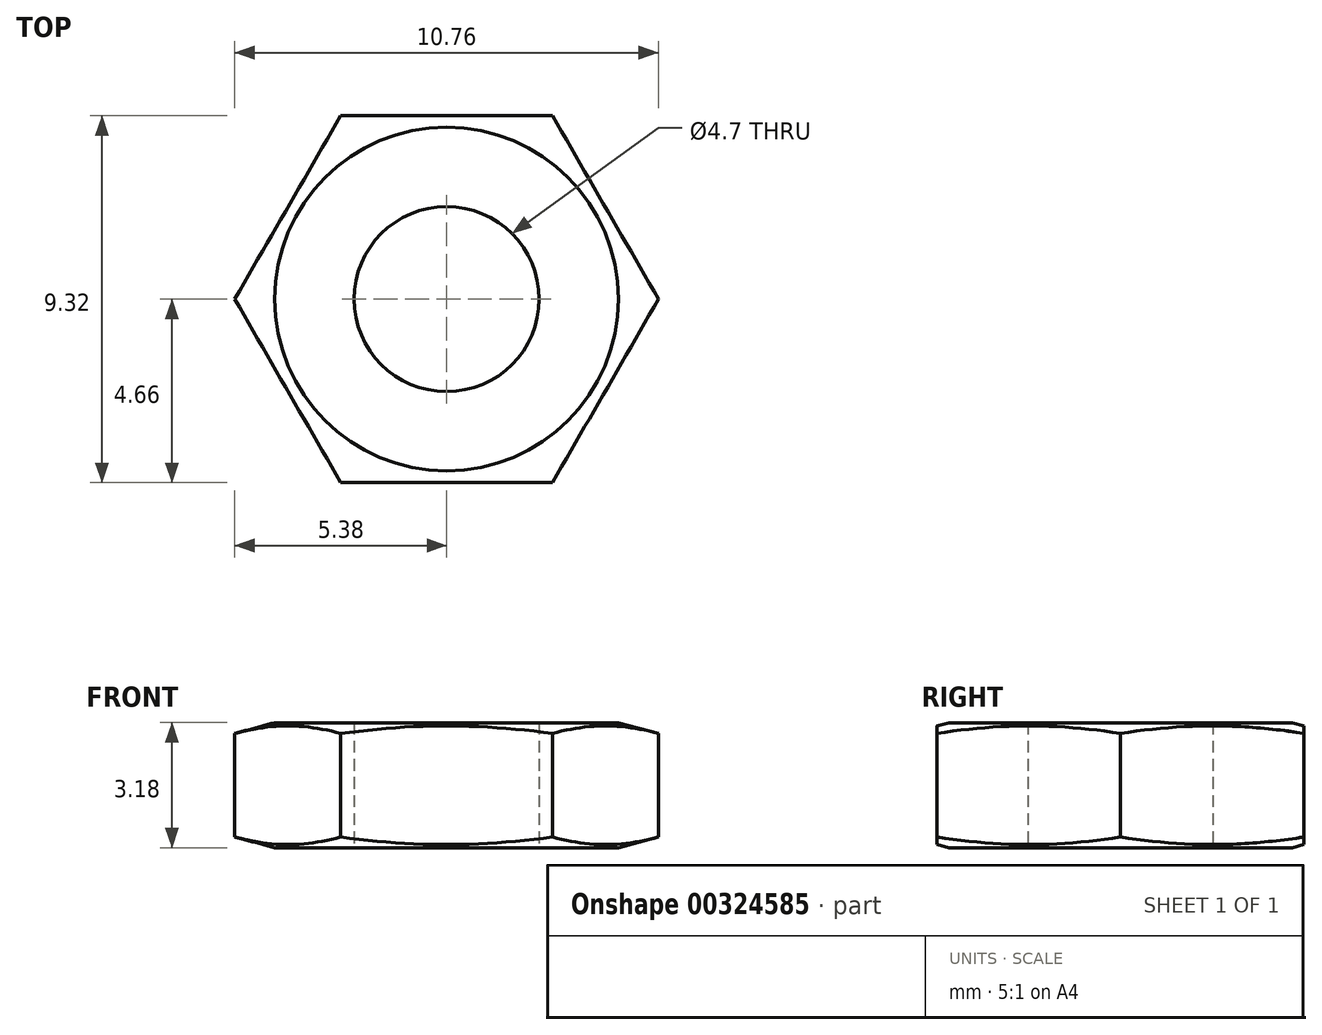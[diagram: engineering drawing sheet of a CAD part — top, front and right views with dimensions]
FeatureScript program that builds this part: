
annotation { "Feature Type Name" : "Feature", "Feature Type Description" : "" }
export const myFeature = defineFeature(function(context is Context, id is Id, definition is map)
    precondition{}
    {
        {
            var Q0;
            Q0=qCreatedBy(makeId("Top.planeOp"),FACE);
            var sketch = newSketch(context, id + "F0", { "sketchPlane" : qUnion([Q0])});
            skCircle(sketch, "E0.cCircle", {"center": v(0, 0) * mm, "radius": 4.66 * mm, "construction": true});
            skLineSegment(sketch, "E0.0", {"start": v(2.7, 4.66) * mm, "end": v(5.38, 0) * mm});
            skLineSegment(sketch, "E0.1", {"start": v(5.38, 0) * mm, "end": v(2.7, -4.66) * mm});
            skLineSegment(sketch, "E0.2", {"start": v(2.7, -4.66) * mm, "end": v(-2.7, -4.66) * mm});
            skLineSegment(sketch, "E0.3", {"start": v(-2.7, -4.66) * mm, "end": v(-5.38, 0) * mm});
            skLineSegment(sketch, "E0.4", {"start": v(-5.38, 0) * mm, "end": v(-2.7, 4.66) * mm});
            skLineSegment(sketch, "E0.5", {"start": v(-2.7, 4.66) * mm, "end": v(2.7, 4.66) * mm});
            skPoint(sketch, "E0.0.midPoint", {"position": v(4.04, 2.33) * mm});
            skCircle(sketch, "E1", {"center": v(0, 0) * mm, "radius": 2.35 * mm});
            skSolve(sketch);
        }
        {
            var Q0;
            Q0=makeQuery(id+"F0.imprint","IMPRINT",FACE,{"disambiguationData":[TD([[makeQuery(id+"F0.imprint","IMPRINT",EDGE,{"derivedFrom":sQuery(id+"F0.wireOp",EDGE,"E0.0")}),-1.0]])]});
            extrude(context, id + "F1", {"entities" : qUnion([Q0]), "endBound" : BoundingType.SYMMETRIC, "depth" : 3.17 * mm});
        }
        {
            var Q0;
            Q0=qCreatedBy(makeId("Front.planeOp"),FACE);
            var sketch = newSketch(context, id + "F2", { "sketchPlane" : qUnion([Q0])});
            skLineSegment(sketch, "E2", {"start": v(4.37, 1.59) * mm, "end": v(5.38, 1.32) * mm});
            skLineSegment(sketch, "E3", {"start": v(5.38, 1.32) * mm, "end": v(5.38, 1.59) * mm});
            skLineSegment(sketch, "E4", {"start": v(5.38, 1.59) * mm, "end": v(4.37, 1.59) * mm});
            skLineSegment(sketch, "E5", {"start": v(0, 1.59) * mm, "end": v(0, -1.59) * mm, "construction": true});
            skSolve(sketch);
        }
        {
            var Q0;
            Q0 = qSketchRegion(id + "F2", true);
            var Q1;
            Q1=sQuery(id+"F2.wireOp",EDGE,"E5");
            revolve(context, id + "F3", {"operationType" : NewBodyOperationType.REMOVE, "entities" : qUnion([Q0]), "axis" : qUnion([Q1]), "revolveType" : RevolveType.FULL, "oppositeDirection" : true});
        }
        {
            var Q0;
            Q0=makeQuery(id+"F1.opExtrude","SWEPT_BODY",BODY,{"disambiguationData":[OSD([sQuery(id+"F0.wireOp",EDGE,"E0.0"),sQuery(id+"F0.wireOp",EDGE,"E0.1"),sQuery(id+"F0.wireOp",EDGE,"E0.2"),sQuery(id+"F0.wireOp",EDGE,"E0.3"),sQuery(id+"F0.wireOp",EDGE,"E0.4"),sQuery(id+"F0.wireOp",EDGE,"E0.5"),sQuery(id+"F0.wireOp",EDGE,"E1")])]});
            var Q1;
            Q1=qCreatedBy(makeId("Top.planeOp"),FACE);
            mirror(context, id + "F4", {"operationType" : NewBodyOperationType.INTERSECT, "entities" : qUnion([Q0]), "mirrorPlane" : qUnion([Q1])});
        }
    });
